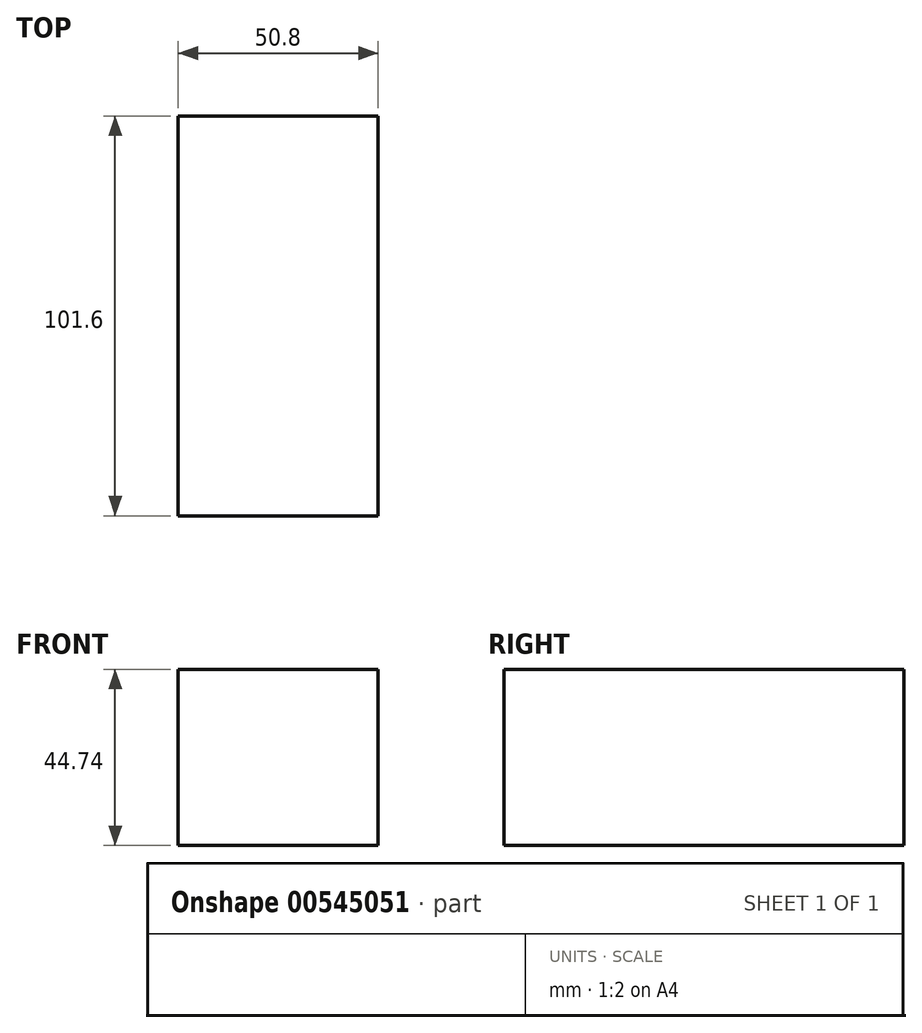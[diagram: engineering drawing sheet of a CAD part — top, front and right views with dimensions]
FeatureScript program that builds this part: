
annotation { "Feature Type Name" : "Feature", "Feature Type Description" : "" }
export const myFeature = defineFeature(function(context is Context, id is Id, definition is map)
    precondition{}
    {
        {
            var Q0;
            Q0=qCreatedBy(makeId("Top.planeOp"),FACE);
            var sketch = newSketch(context, id + "F0", { "sketchPlane" : qUnion([Q0])});
            skLineSegment(sketch, "E0.bottom", {"start": v(0, 50.8) * mm, "end": v(50.8, 50.8) * mm});
            skLineSegment(sketch, "E0.top", {"start": v(0, -50.8) * mm, "end": v(50.8, -50.8) * mm});
            skLineSegment(sketch, "E0.left", {"start": v(0, 50.8) * mm, "end": v(0, -50.8) * mm});
            skLineSegment(sketch, "E0.right", {"start": v(50.8, 50.8) * mm, "end": v(50.8, -50.8) * mm});
            skSolve(sketch);
        }
        {
            var Q0;
            Q0=makeQuery(id+"F0.imprint","IMPRINT",FACE,{"disambiguationData":[TD([[makeQuery(id+"F0.imprint","IMPRINT",EDGE,{"derivedFrom":sQuery(id+"F0.wireOp",EDGE,"E0.bottom")}),-1.0]])]});
            extrude(context, id + "F1", {"entities" : qUnion([Q0]), "depth" : 44.74 * mm, "offsetDistance" : 25.4 * mm});
        }
    });
